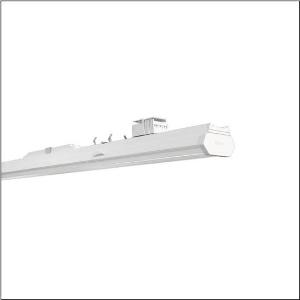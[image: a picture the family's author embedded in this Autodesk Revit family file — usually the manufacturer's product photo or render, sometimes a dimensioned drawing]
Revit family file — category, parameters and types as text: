
# Revit family: licross_r__11_protected_mo_51td12dn495g_4259
name_source: partatom
category: Lighting Fixtures
units: mm (PartAtom-declared; Revit-internal decimal feet)

## family parameters
Cut with Voids When Loaded = No
Host = Face
Light Source = No
Part Type = Normal
Room Calculation Point = No
Round Connector Dimension = Use Diameter
Shared = No

## types (1)
- --- (1 x LED, 9980 lm, 57.1 W, 4000K)
    Apparent Load = 57 VA
    CIE Flux Codes = 73 92 98 99 100
    Color Rendering = 80
    Color Temperature = 4000K
    Default Elevation = 1800 mm
    Description = Licross® 11 Protected MO, luminaire insert, of sheet steel, galvanised, coil coated, white, length: 1.500mm, width: 90mm, height: 101mm, LED rated luminous flux: 9.980lm, light colour: 840, control gear: DALI 2, with plug, 5-pole, with phase selection, mains connection: 220..240V, AC, 50/60Hz, rated input power: 57W, halogen-free wiring, primary optical cover: cover, of PMMA, light emission: direct distribution, primary light characteristic: symmetric, protection rating (complete): IP54, insulation class (complete): insulation class I (protective earthing), certification: CE, ENEC, VDE, UKCA, protection symbol: D if used in an environment with non-conductive dust loads with corresponding accessories, impact resistance: IK06, permissible ambient temperature for indoor applications: -25..+35°C, corresponds to IFS (International Featured Standards) requirements for safety and quality in the food industry, reducing of maximum allowable ambient temperature of 5°C with ceiling mounting, LABS conformity tested according to VDMA 24364:2018-05, packaging unit: 1 piece
    Height = 92 mm
    Lamp = 1 x LED
    Lamp Light Flux = 9980 lm
    Lamp Power = 57.1 W
    Lamp count = 1
    Length = 1500 mm
    Luminous efficacy = 175 lm/W
    Manufacturer = Siteco
    ModVariant = No
    Model = 51TD12DN495G
    Mounting Place = Ceiling
    Mounting Type = Pendant
    Number of Poles = 1
    OnlyDefault = Yes
    Power Factor = 1
    Product Name = Licross® 11 Protected MO
    Product group = luminaire insert
    ProductGroupID = 901
    Protection Class = Protection class I
    Protection Degree = IP 54
    RLX_Detail_Level = 1
    RLX_Emergency_Light_Flux = 0 lm
    RLX_Emergency_Type = 0
    RLX_Emergency_Type_DB = No
    RlxData = <blob elided: 24445 chars, md5=8dda0120>
    Socket = socket
    Standby Power = 0 W
    System Light Flux = 9980 lm
    System Power = 57 W
    Type Comments = factory setting: luminous flux: 100 % | dim-lin: 254 | 378 mA
    Type Image = l_1256145.jpg
    URL = http://relux.com
    VarID = @adj_031267
    Voltage = 0 V
    Weight = 0.00 kg
    Width = 88 mm

## geometry (parser evidence)
native form markers: Blend x4, Sweep x10
no freeform markers — native parametric forms only
